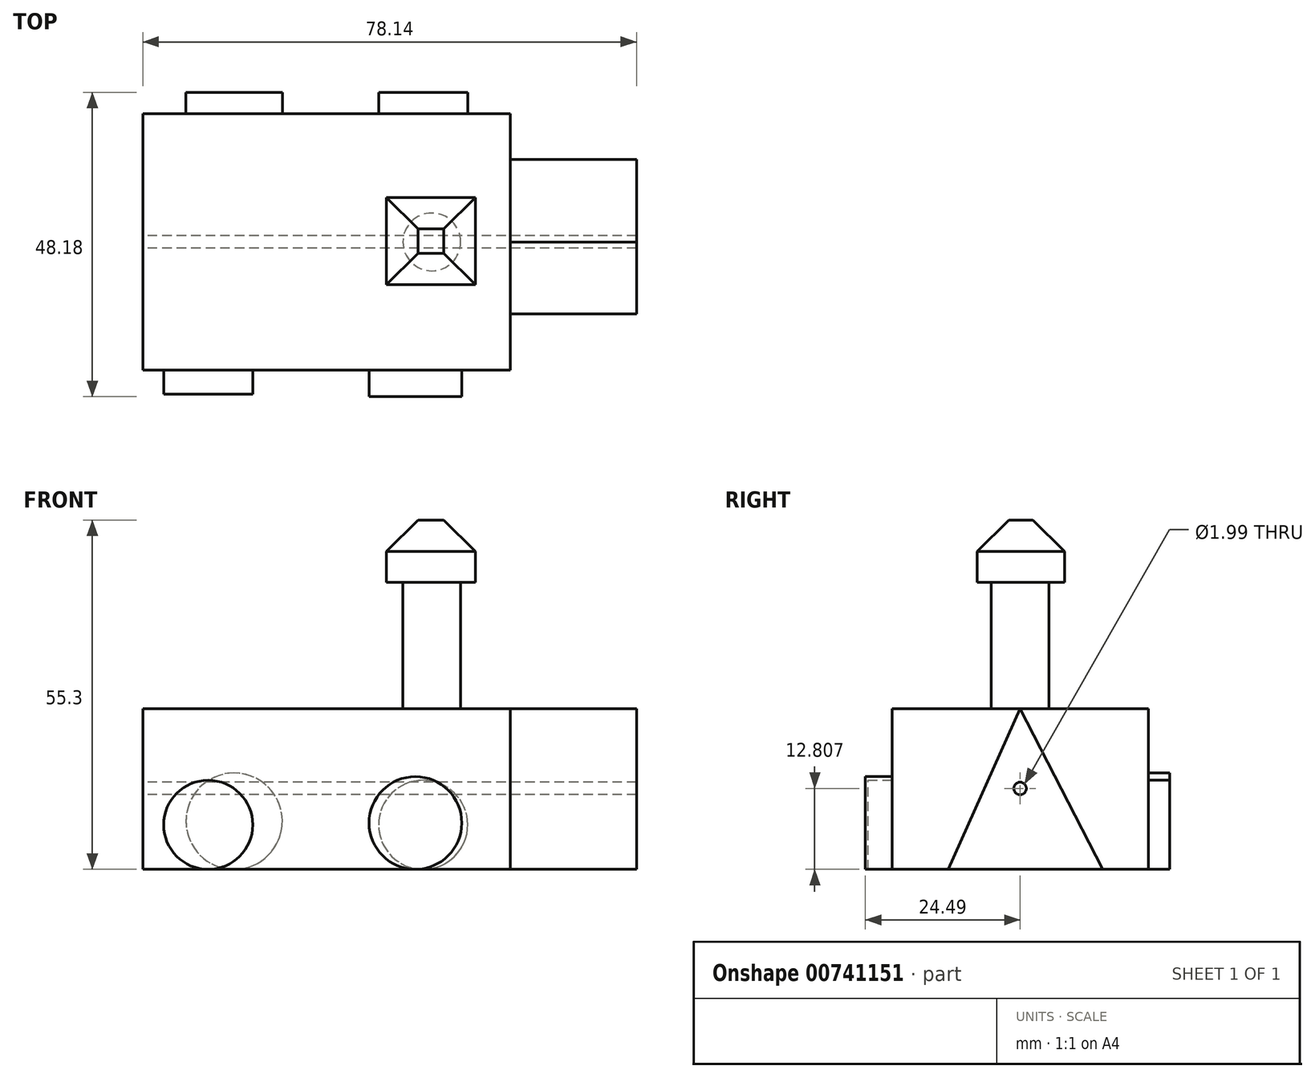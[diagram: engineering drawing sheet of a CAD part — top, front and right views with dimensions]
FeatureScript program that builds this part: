
annotation { "Feature Type Name" : "Feature", "Feature Type Description" : "" }
export const myFeature = defineFeature(function(context is Context, id is Id, definition is map)
    precondition{}
    {
        {
            var Q0;
            Q0=qCreatedBy(makeId("Top.planeOp"),FACE);
            var sketch = newSketch(context, id + "F0", { "sketchPlane" : qUnion([Q0])});
            skLineSegment(sketch, "E0.bottom", {"start": v(-27.49, 20.3) * mm, "end": v(30.65, 20.3) * mm});
            skLineSegment(sketch, "E0.top", {"start": v(-27.49, -20.3) * mm, "end": v(30.65, -20.3) * mm});
            skLineSegment(sketch, "E0.left", {"start": v(-27.49, 20.3) * mm, "end": v(-27.49, -20.3) * mm});
            skLineSegment(sketch, "E0.right", {"start": v(30.65, 20.3) * mm, "end": v(30.65, -20.3) * mm});
            skSolve(sketch);
        }
        {
            var Q0;
            Q0 = qSketchRegion(id + "F0", true);
            extrude(context, id + "F1", {"entities" : qUnion([Q0]), "depth" : 25.4 * mm, "offsetDistance" : 25.4 * mm});
        }
        {
            var Q0;
            Q0=makeQuery(id+"F1.opExtrude","SWEPT_FACE",FACE,{"disambiguationData":[OSD([sQuery(id+"F0.wireOp",EDGE,"E0.right")])]});
            var sketch = newSketch(context, id + "F2", { "sketchPlane" : qUnion([Q0])});
            skLineSegment(sketch, "E1", {"start": v(0, 25.4) * mm, "end": v(13.1, 0) * mm});
            skLineSegment(sketch, "E2", {"start": v(0, 25.4) * mm, "end": v(-11.37, 0) * mm});
            skLineSegment(sketch, "E3", {"start": v(-126.2, 25.4) * mm, "end": v(-103.18, 5.61) * mm});
            skSolve(sketch);
        }
        {
            var Q0;
            {var subQ0=sQuery(id+"F2.wireOp",EDGE,"E1");Q0=makeQuery(id+"F2.imprint","IMPRINT",FACE,{"disambiguationData":[TD([[makeQuery(id+"F2.imprint","IMPRINT",EDGE,{"derivedFrom":subQ0}),-1.0]])]});}
            extrude(context, id + "F3", {"entities" : qUnion([Q0]), "operationType" : NewBodyOperationType.ADD, "depth" : 20 * mm, "offsetDistance" : 25.4 * mm});
        }
        {
            var Q0;
            Q0=makeQuery(id+"F1.opExtrude","CAP_FACE",FACE,{"disambiguationData":[OSD([sQuery(id+"F0.wireOp",EDGE,"E0.bottom"),sQuery(id+"F0.wireOp",EDGE,"E0.top"),sQuery(id+"F0.wireOp",EDGE,"E0.left"),sQuery(id+"F0.wireOp",EDGE,"E0.right")])],"isStart":false});
            var sketch = newSketch(context, id + "F4", { "sketchPlane" : qUnion([Q0])});
            skCircle(sketch, "E4", {"center": v(18.24, 0) * mm, "radius": 4.57 * mm});
            skSolve(sketch);
        }
        {
            var Q0;
            Q0 = qSketchRegion(id + "F4", true);
            extrude(context, id + "F5", {"entities" : qUnion([Q0]), "operationType" : NewBodyOperationType.ADD, "depth" : 20 * mm, "offsetDistance" : 25 * mm});
        }
        {
            var Q0;
            Q0=makeQuery(id+"F5.opExtrude","CAP_FACE",FACE,{"disambiguationData":[OSD([sQuery(id+"F4.wireOp",EDGE,"E4")])],"isStart":false});
            var sketch = newSketch(context, id + "F6", { "sketchPlane" : qUnion([Q0])});
            skLineSegment(sketch, "E5.bottom", {"start": v(11.04, 7.05) * mm, "end": v(25.15, 7.05) * mm});
            skLineSegment(sketch, "E5.top", {"start": v(11.04, -6.76) * mm, "end": v(25.15, -6.76) * mm});
            skLineSegment(sketch, "E5.left", {"start": v(11.04, 7.05) * mm, "end": v(11.04, -6.76) * mm});
            skLineSegment(sketch, "E5.right", {"start": v(25.15, 7.05) * mm, "end": v(25.15, -6.76) * mm});
            skSolve(sketch);
        }
        {
            var Q0;
            Q0 = qSketchRegion(id + "F6", true);
            extrude(context, id + "F7", {"entities" : qUnion([Q0]), "operationType" : NewBodyOperationType.ADD, "depth" : 9.9 * mm, "offsetDistance" : 25 * mm});
        }
        {
            var Q0;
            Q0=makeQuery(id+"F7.opExtrude","CAP_FACE",FACE,{"disambiguationData":[OSD([sQuery(id+"F6.wireOp",EDGE,"E5.bottom"),sQuery(id+"F6.wireOp",EDGE,"E5.top"),sQuery(id+"F6.wireOp",EDGE,"E5.left"),sQuery(id+"F6.wireOp",EDGE,"E5.right")])],"isStart":false});
            chamfer(context, id + "F8", {"entities" : qUnion([Q0]), "width" : 5 * mm, "tangentPropagation" : true});
        }
        {
            var Q0;
            Q0=makeQuery(id+"F1.opExtrude","SWEPT_FACE",FACE,{"disambiguationData":[OSD([sQuery(id+"F0.wireOp",EDGE,"E0.top")])]});
            var sketch = newSketch(context, id + "F9", { "sketchPlane" : qUnion([Q0])});
            skCircle(sketch, "E6", {"center": v(-17.16, 7.05) * mm, "radius": 7.05 * mm});
            skCircle(sketch, "E7", {"center": v(13.92, 7.34) * mm, "radius": 7.34 * mm});
            skSolve(sketch);
        }
        {
            var Q0;
            Q0=makeQuery(id+"F9.imprint","IMPRINT",FACE,{"disambiguationData":[TD([[makeQuery(id+"F9.imprint","IMPRINT",EDGE,{"derivedFrom":sQuery(id+"F9.wireOp",EDGE,"E6")}),1.0]])]});
            extrude(context, id + "F10", {"entities" : qUnion([Q0]), "operationType" : NewBodyOperationType.ADD, "depth" : 3.8 * mm, "offsetDistance" : 25 * mm});
        }
        {
            var Q0;
            Q0=makeQuery(id+"F1.opExtrude","SWEPT_FACE",FACE,{"disambiguationData":[OSD([sQuery(id+"F0.wireOp",EDGE,"E0.top")])]});
            var sketch = newSketch(context, id + "F11", { "sketchPlane" : qUnion([Q0])});
            skCircle(sketch, "E8", {"center": v(15.65, 7.34) * mm, "radius": 7.34 * mm});
            skSolve(sketch);
        }
        {
            var Q0;
            Q0=makeQuery(id+"F11.imprint","IMPRINT",FACE,{"disambiguationData":[TD([[makeQuery(id+"F11.imprint","IMPRINT",EDGE,{"derivedFrom":sQuery(id+"F11.wireOp",EDGE,"E8")}),1.0]])]});
            extrude(context, id + "F12", {"entities" : qUnion([Q0]), "operationType" : NewBodyOperationType.ADD, "depth" : 4.2 * mm, "offsetDistance" : 25 * mm});
        }
        {
            var Q0;
            Q0=makeQuery(id+"F1.opExtrude","SWEPT_FACE",FACE,{"disambiguationData":[OSD([sQuery(id+"F0.wireOp",EDGE,"E0.bottom")])]});
            var sketch = newSketch(context, id + "F13", { "sketchPlane" : qUnion([Q0])});
            skCircle(sketch, "E9", {"center": v(-16.87, 7.05) * mm, "radius": 7.05 * mm});
            skSolve(sketch);
        }
        {
            var Q0;
            Q0=makeQuery(id+"F13.imprint","IMPRINT",FACE,{"disambiguationData":[TD([[makeQuery(id+"F13.imprint","IMPRINT",EDGE,{"derivedFrom":sQuery(id+"F13.wireOp",EDGE,"E9")}),1.0]])]});
            extrude(context, id + "F14", {"entities" : qUnion([Q0]), "operationType" : NewBodyOperationType.ADD, "depth" : 3.4 * mm, "offsetDistance" : 25 * mm});
        }
        {
            var Q0;
            Q0=makeQuery(id+"F1.opExtrude","SWEPT_FACE",FACE,{"disambiguationData":[OSD([sQuery(id+"F0.wireOp",EDGE,"E0.bottom")])]});
            var sketch = newSketch(context, id + "F15", { "sketchPlane" : qUnion([Q0])});
            skCircle(sketch, "E10", {"center": v(13.06, 7.63) * mm, "radius": 7.63 * mm});
            skSolve(sketch);
        }
        {
            var Q0;
            Q0=makeQuery(id+"F15.imprint","IMPRINT",FACE,{"disambiguationData":[TD([[makeQuery(id+"F15.imprint","IMPRINT",EDGE,{"derivedFrom":sQuery(id+"F15.wireOp",EDGE,"E10")}),1.0]])]});
            extrude(context, id + "F16", {"entities" : qUnion([Q0]), "operationType" : NewBodyOperationType.ADD, "depth" : 3.4 * mm, "offsetDistance" : 25 * mm});
        }
        {
            var Q0;
            Q0=makeQuery(id+"F1.opExtrude","SWEPT_FACE",FACE,{"disambiguationData":[OSD([sQuery(id+"F0.wireOp",EDGE,"E0.left")])]});
            var sketch = newSketch(context, id + "F17", { "sketchPlane" : qUnion([Q0])});
            skCircle(sketch, "E11", {"center": v(0, 12.8) * mm, "radius": 2.5 * mm});
            skSolve(sketch);
        }
        {
            var Q0;
            Q0=sQuery(id+"F17.wireOp",VERTEX,"E11.center");
            var Q1;
            Q1=makeQuery(id+"F1.opExtrude","SWEPT_BODY",BODY,{"disambiguationData":[OSD([sQuery(id+"F0.wireOp",EDGE,"E0.bottom"),sQuery(id+"F0.wireOp",EDGE,"E0.top"),sQuery(id+"F0.wireOp",EDGE,"E0.left"),sQuery(id+"F0.wireOp",EDGE,"E0.right")])]});
            hole(context, id + "F18", {"style" : HoleStyle.SIMPLE, "endStyle" : HoleEndStyle.THROUGH, "standardTappedOrClearance" : lookupTablePath({ "standard" : "ANSI", "engagement" : "75%", "pitch" : "48 tpi", "size" : "#3", "type" : "Tapped" }), "standardBlindInLast" : lookupTablePath({ "standard" : "ANSI", "engagement" : "75%", "pitch" : "48 tpi", "size" : "#3", "type" : "Tapped" }), "holeDiameter" : 2 * mm, "majorDiameter" : 2.5 * mm, "showTappedDepth" : true, "tappedDepth" : 20 * mm, "tapClearance" : 3, "locations" : qUnion([Q0]), "scope" : qUnion([Q1])});
        }
    });
